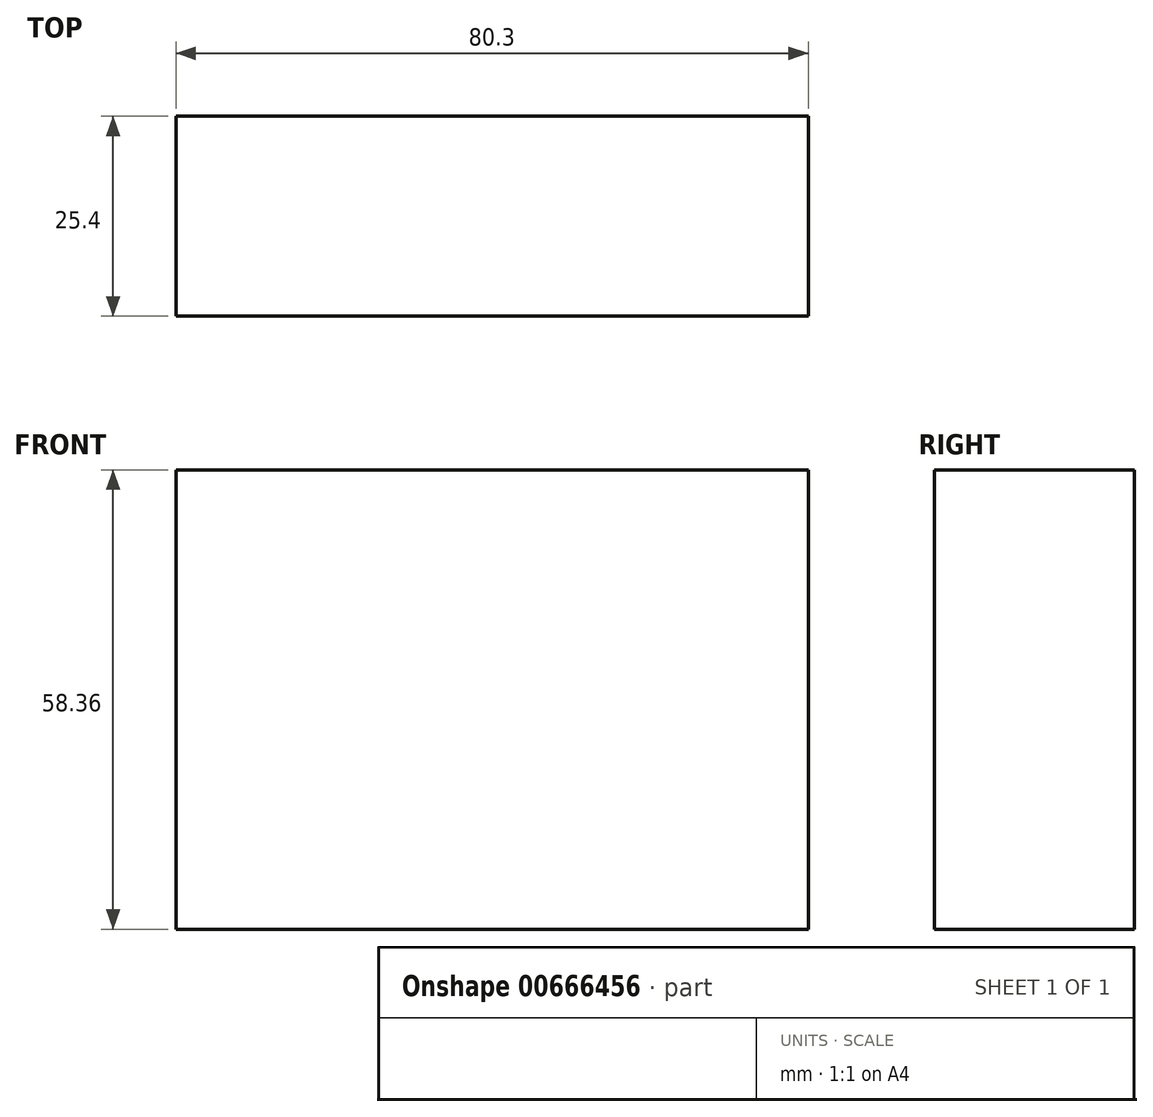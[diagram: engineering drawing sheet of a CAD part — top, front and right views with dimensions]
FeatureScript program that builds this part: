
annotation { "Feature Type Name" : "Feature", "Feature Type Description" : "" }
export const myFeature = defineFeature(function(context is Context, id is Id, definition is map)
    precondition{}
    {
        {
            var Q0;
            Q0=qCreatedBy(makeId("Front.planeOp"),FACE);
            var sketch = newSketch(context, id + "F0", { "sketchPlane" : qUnion([Q0])});
            skLineSegment(sketch, "E0.bottom", {"start": v(-55.96, 48.54) * mm, "end": v(24.34, 48.54) * mm});
            skLineSegment(sketch, "E0.top", {"start": v(-55.96, -9.82) * mm, "end": v(24.34, -9.82) * mm});
            skLineSegment(sketch, "E0.left", {"start": v(-55.96, 48.54) * mm, "end": v(-55.96, -9.82) * mm});
            skLineSegment(sketch, "E0.right", {"start": v(24.34, 48.54) * mm, "end": v(24.34, -9.82) * mm});
            skSolve(sketch);
        }
        {
            var Q0;
            Q0=makeQuery(id+"F0.imprint","IMPRINT",FACE,{"disambiguationData":[TD([[makeQuery(id+"F0.imprint","IMPRINT",EDGE,{"derivedFrom":sQuery(id+"F0.wireOp",EDGE,"E0.bottom")}),-1.0]])]});
            extrude(context, id + "F1", {"entities" : qUnion([Q0]), "depth" : 25.4 * mm, "offsetDistance" : 25.4 * mm});
        }
    });
